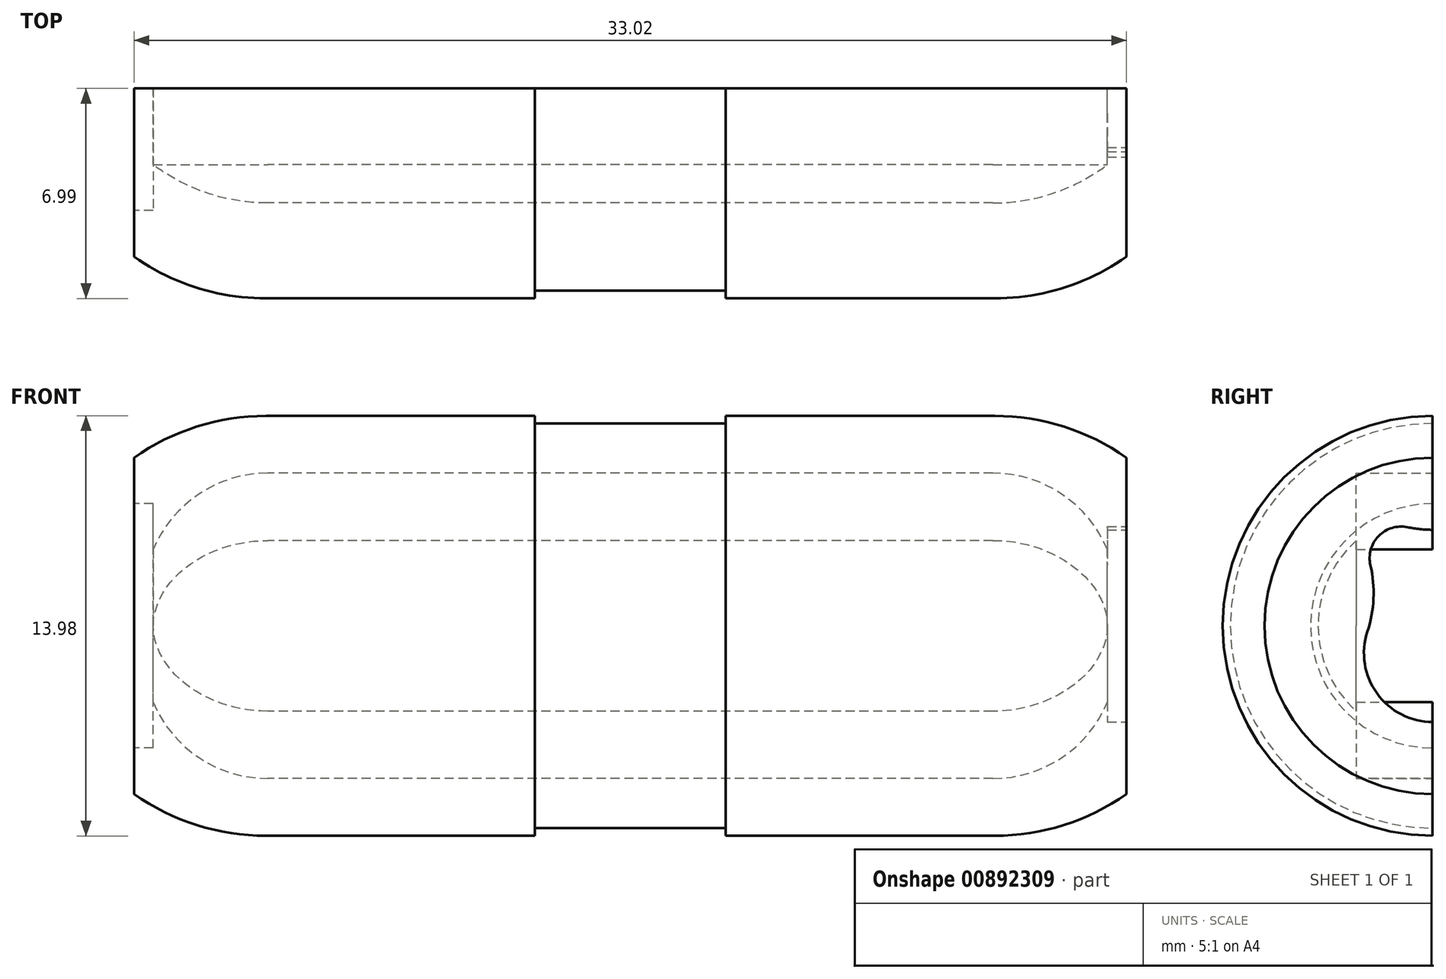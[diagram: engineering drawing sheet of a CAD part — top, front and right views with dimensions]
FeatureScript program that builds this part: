
annotation { "Feature Type Name" : "Feature", "Feature Type Description" : "" }
export const myFeature = defineFeature(function(context is Context, id is Id, definition is map)
    precondition{}
    {
        {
            var Q0;
            Q0=qCreatedBy(makeId("Front.planeOp"),FACE);
            var sketch = newSketch(context, id + "F0", { "sketchPlane" : qUnion([Q0])});
            skLineSegment(sketch, "E0.top", {"start": v(12.12, 6.99) * mm, "end": v(-12.12, 6.99) * mm});
            skPoint(sketch, "E0.middle", {"position": v(0, 0) * mm});
            skArc(sketch, "E1.filletArc", {"start": v(-12.12, 6.99) * mm, "mid": v(-16.24, 5.78) * mm, "end": v(-19.05, 2.54) * mm});
            skArc(sketch, "E2.filletArc", {"start": v(19.05, 2.54) * mm, "mid": v(16.24, 5.78) * mm, "end": v(12.12, 6.99) * mm});
            skLineSegment(sketch, "E3.top", {"start": v(12.07, 3.81) * mm, "end": v(-12.07, 3.81) * mm});
            skArc(sketch, "E4.filletArc", {"start": v(-12.07, 3.81) * mm, "mid": v(-14.07, 3.48) * mm, "end": v(-15.88, 2.54) * mm});
            skArc(sketch, "E5.filletArc", {"start": v(15.88, 2.54) * mm, "mid": v(14.07, 3.48) * mm, "end": v(12.07, 3.81) * mm});
            skLineSegment(sketch, "E6.top", {"start": v(-19.05, 2.54) * mm, "end": v(-15.88, 2.54) * mm});
            skLineSegment(sketch, "E7.trimOffspring", {"start": v(15.88, 2.54) * mm, "end": v(19.05, 2.54) * mm});
            skSolve(sketch);
        }
        {
            var Q0;
            Q0=qCreatedBy(makeId("Top.planeOp"),FACE);
            var sketch = newSketch(context, id + "F1", { "sketchPlane" : qUnion([Q0])});
            skLineSegment(sketch, "E8", {"start": v(-41.86, 0) * mm, "end": v(38.58, 0) * mm, "construction": true});
            skSolve(sketch);
        }
        {
            var Q0;
            Q0=qSketchRegion(id+"F0",true);
            var Q1;
            Q1=sQuery(id+"F1.wireOp",EDGE,"E8");
            revolve(context, id + "F2", {"surfaceOperationType" : NewSurfaceOperationType.NEW, "entities" : qUnion([Q0]), "axis" : qUnion([Q1]), "revolveType" : RevolveType.ONE_DIRECTION, "angle" : 180 * degree});
        }
        {
            var Q0;
            Q0=makeQuery(id+"F2.opRevolve","CAP_FACE",FACE,{"disambiguationData":[OSD([sQuery(id+"F0.wireOp",EDGE,"E0.top"),sQuery(id+"F0.wireOp",EDGE,"E1.filletArc"),sQuery(id+"F0.wireOp",EDGE,"E2.filletArc"),sQuery(id+"F0.wireOp",EDGE,"E3.top"),sQuery(id+"F0.wireOp",EDGE,"E4.filletArc"),sQuery(id+"F0.wireOp",EDGE,"E5.filletArc"),sQuery(id+"F0.wireOp",EDGE,"JIvlJlBu-vfLA-I6Gr-C8jU-59FBPmd7U8bv"),sQuery(id+"F0.wireOp",EDGE,"RInppC3X-QeJU-EZpC-KpJT-0cWvms3T49e7")])],"isStart":true});
            var sketch = newSketch(context, id + "F3", { "sketchPlane" : qUnion([Q0])});
            skPoint(sketch, "E9.middle", {"position": v(0, 0) * mm});
            skLineSegment(sketch, "E10", {"start": v(12.07, -3.8) * mm, "end": v(-12.07, -3.81) * mm});
            skLineSegment(sketch, "E11", {"start": v(-12.07, -3.81) * mm, "end": v(-12.07, -3.81) * mm});
            skLineSegment(sketch, "E12", {"start": v(-19.05, -12.7) * mm, "end": v(-19.05, -12.7) * mm});
            skArc(sketch, "E13", {"start": v(-12.07, -3.81) * mm, "mid": v(-14.07, -3.48) * mm, "end": v(-15.88, -2.54) * mm});
            skLineSegment(sketch, "E14", {"start": v(-12.07, -5.08) * mm, "end": v(12.07, -5.08) * mm});
            skLineSegment(sketch, "E15", {"start": v(-15.88, -2.54) * mm, "end": v(-15.88, -2.54) * mm});
            skPoint(sketch, "E16.visualSharp", {"position": v(-14.82, -5.08) * mm});
            skArc(sketch, "E16.filletArc", {"start": v(-15.88, -2.54) * mm, "mid": v(-14.35, -4.39) * mm, "end": v(-12.07, -5.08) * mm});
            skPoint(sketch, "E17.visualSharp", {"position": v(22.86, -7.62) * mm});
            skArc(sketch, "E17.filletArc", {"start": v(12.07, -5.08) * mm, "mid": v(14.35, -4.38) * mm, "end": v(15.88, -2.54) * mm});
            skArc(sketch, "E18", {"start": v(12.07, -3.81) * mm, "mid": v(14.07, -3.48) * mm, "end": v(15.88, -2.54) * mm});
            skArc(sketch, "E19.MirrorCS", {"start": v(12.07, 5.08) * mm, "mid": v(14.35, 4.38) * mm, "end": v(15.88, 2.54) * mm});
            skArc(sketch, "E20.MirrorCS", {"start": v(12.07, 3.81) * mm, "mid": v(14.07, 3.48) * mm, "end": v(15.88, 2.54) * mm});
            skLineSegment(sketch, "E21.MirrorCS", {"start": v(12.07, 3.8) * mm, "end": v(-12.07, 3.81) * mm});
            skLineSegment(sketch, "E22.MirrorCS", {"start": v(-12.07, 5.08) * mm, "end": v(12.07, 5.08) * mm});
            skArc(sketch, "E23.MirrorCS", {"start": v(-15.88, 2.54) * mm, "mid": v(-14.35, 4.39) * mm, "end": v(-12.07, 5.08) * mm});
            skArc(sketch, "E24.MirrorCS", {"start": v(-12.07, 3.81) * mm, "mid": v(-14.07, 3.48) * mm, "end": v(-15.88, 2.54) * mm});
            skSolve(sketch);
        }
        {
            var Q0;
            Q0=qSketchRegion(id+"F3",true);
            extrude(context, id + "F4", {"entities" : qUnion([Q0]), "operationType" : NewBodyOperationType.REMOVE, "oppositeDirection" : true, "depth" : 2.54 * mm, "offsetDistance" : 25.4 * mm});
        }
        {
            var Q0;
            Q0=qCreatedBy(makeId("Front.planeOp"),FACE);
            var sketch = newSketch(context, id + "F5", { "sketchPlane" : qUnion([Q0])});
            skLineSegment(sketch, "E25", {"start": v(48.97, 0) * mm, "end": v(-50.21, 0) * mm, "construction": true});
            skSolve(sketch);
        }
        {
            var Q0;
            Q0=makeQuery(id+"F2.opRevolve","CAP_FACE",FACE,{"disambiguationData":[OSD([sQuery(id+"F0.wireOp",EDGE,"E0.top"),sQuery(id+"F0.wireOp",EDGE,"E1.filletArc"),sQuery(id+"F0.wireOp",EDGE,"E2.filletArc"),sQuery(id+"F0.wireOp",EDGE,"E3.top"),sQuery(id+"F0.wireOp",EDGE,"E4.filletArc"),sQuery(id+"F0.wireOp",EDGE,"E5.filletArc"),sQuery(id+"F0.wireOp",EDGE,"E6.top"),sQuery(id+"F0.wireOp",EDGE,"E7.trimOffspring")])],"isStart":true});
            var sketch = newSketch(context, id + "F6", { "sketchPlane" : qUnion([Q0])});
            skLineSegment(sketch, "E26.bottom", {"start": v(3.18, 6.73) * mm, "end": v(-3.17, 6.73) * mm});
            skLineSegment(sketch, "E26.top", {"start": v(3.18, 7.24) * mm, "end": v(-3.17, 7.24) * mm});
            skLineSegment(sketch, "E26.left", {"start": v(3.18, 6.73) * mm, "end": v(3.18, 7.24) * mm});
            skLineSegment(sketch, "E26.right", {"start": v(-3.17, 6.73) * mm, "end": v(-3.17, 7.24) * mm});
            skPoint(sketch, "E26.middle", {"position": v(0, 6.99) * mm});
            skSolve(sketch);
        }
        {
            var Q0;
            Q0 = qSketchRegion(id + "F6", true);
            var Q1;
            Q1=sQuery(id+"F5.wireOp",EDGE,"E25");
            revolve(context, id + "F7", {"operationType" : NewBodyOperationType.REMOVE, "surfaceOperationType" : NewSurfaceOperationType.NEW, "entities" : qUnion([Q0]), "axis" : qUnion([Q1]), "revolveType" : RevolveType.FULL, "oppositeDirection" : true});
        }
        {
            var Q0;
            Q0=makeQuery(id+"F4.boolean.opBoolean","COPY",FACE,{"derivedFrom":makeQuery(id+"F4.opExtrude","CAP_FACE",FACE,{"disambiguationData":[OSD([sQuery(id+"F3.wireOp",EDGE,"E10"),sQuery(id+"F3.wireOp",EDGE,"E13"),sQuery(id+"F3.wireOp",EDGE,"E14"),sQuery(id+"F3.wireOp",EDGE,"L3rBEucQ-c3uq-OMWU-wc5G-qcBvpzBimpHX"),sQuery(id+"F3.wireOp",EDGE,"E16.filletArc"),sQuery(id+"F3.wireOp",EDGE,"19001bea-0d48-4adf-b7b1-09b1f723019d.filletArc")])],"isStart":false})});
            var sketch = newSketch(context, id + "F8", { "sketchPlane" : qUnion([Q0])});
            skLineSegment(sketch, "E27", {"start": v(-12.07, -3.3) * mm, "end": v(12.07, -3.3) * mm});
            skLineSegment(sketch, "E28", {"start": v(12.07, -3.8) * mm, "end": v(-12.07, -3.81) * mm});
            skPoint(sketch, "E29.visualSharp", {"position": v(-22.86, -12.7) * mm});
            skArc(sketch, "E29.filletArc", {"start": v(-15.88, -2.54) * mm, "mid": v(-14.07, -3.48) * mm, "end": v(-12.07, -3.81) * mm});
            skPoint(sketch, "E30.visualSharp", {"position": v(-15.88, -3.56) * mm});
            skArc(sketch, "E30.filletArc", {"start": v(-15.88, -1.78) * mm, "mid": v(-14.1, -2.86) * mm, "end": v(-12.07, -3.3) * mm});
            skPoint(sketch, "E31", {"position": v(-15.88, -1.78) * mm});
            skLineSegment(sketch, "E32", {"start": v(-15.88, -1.78) * mm, "end": v(-15.88, -2.54) * mm});
            skLineSegment(sketch, "E33", {"start": v(15.88, -2.54) * mm, "end": v(15.88, -2.54) * mm});
            skArc(sketch, "E34.filletArc", {"start": v(12.07, -3.8) * mm, "mid": v(14.07, -3.48) * mm, "end": v(15.88, -2.54) * mm});
            skLineSegment(sketch, "E35", {"start": v(15.88, -2.54) * mm, "end": v(15.88, -1.78) * mm});
            skLineSegment(sketch, "E36", {"start": v(12.07, -3.3) * mm, "end": v(12.07, -3.3) * mm});
            skPoint(sketch, "E37.visualSharp", {"position": v(15.88, -3.3) * mm});
            skArc(sketch, "E37.filletArc", {"start": v(12.07, -3.3) * mm, "mid": v(14.12, -2.9) * mm, "end": v(15.88, -1.78) * mm});
            skArc(sketch, "E38.MirrorCS", {"start": v(12.07, 3.8) * mm, "mid": v(14.07, 3.48) * mm, "end": v(15.88, 2.54) * mm});
            skArc(sketch, "E39.MirrorCS", {"start": v(12.07, 3.3) * mm, "mid": v(14.12, 2.9) * mm, "end": v(15.88, 1.78) * mm});
            skLineSegment(sketch, "E40.MirrorCS", {"start": v(15.88, 2.54) * mm, "end": v(15.88, 1.78) * mm});
            skLineSegment(sketch, "E41.MirrorCS", {"start": v(12.07, 3.8) * mm, "end": v(-12.07, 3.81) * mm});
            skLineSegment(sketch, "E42.MirrorCS", {"start": v(-15.88, 1.78) * mm, "end": v(-15.88, 2.54) * mm});
            skLineSegment(sketch, "E43.MirrorCS", {"start": v(-12.07, 3.3) * mm, "end": v(12.07, 3.3) * mm});
            skArc(sketch, "E44.MirrorCS", {"start": v(-15.88, 2.54) * mm, "mid": v(-14.07, 3.48) * mm, "end": v(-12.07, 3.81) * mm});
            skArc(sketch, "E45.MirrorCS", {"start": v(-15.88, 1.78) * mm, "mid": v(-14.1, 2.86) * mm, "end": v(-12.07, 3.3) * mm});
            skSolve(sketch);
        }
        {
            var Q0;
            Q0 = qSketchRegion(id + "F8", true);
            extrude(context, id + "F9", {"entities" : qUnion([Q0]), "operationType" : NewBodyOperationType.REMOVE, "depth" : 2.54 * mm, "offsetDistance" : 25.4 * mm});
        }
        {
            var Q0;
            Q0=makeQuery(id+"F2.opRevolve","CAP_FACE",FACE,{"disambiguationData":[OSD([sQuery(id+"F0.wireOp",EDGE,"E0.top"),sQuery(id+"F0.wireOp",EDGE,"E1.filletArc"),sQuery(id+"F0.wireOp",EDGE,"E2.filletArc"),sQuery(id+"F0.wireOp",EDGE,"E3.top"),sQuery(id+"F0.wireOp",EDGE,"E4.filletArc"),sQuery(id+"F0.wireOp",EDGE,"E5.filletArc"),sQuery(id+"F0.wireOp",EDGE,"E6.top"),sQuery(id+"F0.wireOp",EDGE,"E7.trimOffspring")])],"isStart":true});
            var sketch = newSketch(context, id + "F10", { "sketchPlane" : qUnion([Q0])});
            skLineSegment(sketch, "E46.bottom", {"start": v(-19.05, 5.6) * mm, "end": v(-16.51, 5.6) * mm});
            skLineSegment(sketch, "E46.top", {"start": v(-19.05, -5.6) * mm, "end": v(-16.51, -5.6) * mm});
            skLineSegment(sketch, "E46.left", {"start": v(-19.05, 5.6) * mm, "end": v(-19.05, -5.6) * mm});
            skLineSegment(sketch, "E46.right", {"start": v(-16.51, 5.6) * mm, "end": v(-16.51, -5.6) * mm});
            skLineSegment(sketch, "E47.MirrorCS", {"start": v(19.05, -5.6) * mm, "end": v(16.51, -5.6) * mm});
            skLineSegment(sketch, "E48.MirrorCS", {"start": v(19.05, 5.6) * mm, "end": v(19.05, -5.6) * mm});
            skLineSegment(sketch, "E49.MirrorCS", {"start": v(19.05, 5.6) * mm, "end": v(16.51, 5.6) * mm});
            skLineSegment(sketch, "E50.MirrorCS", {"start": v(16.51, 5.6) * mm, "end": v(16.51, -5.6) * mm});
            skSolve(sketch);
        }
        {
            var Q0;
            Q0 = qSketchRegion(id + "F10", true);
            extrude(context, id + "F11", {"entities" : qUnion([Q0]), "operationType" : NewBodyOperationType.REMOVE, "oppositeDirection" : true, "depth" : 25.4 * mm, "offsetDistance" : 25.4 * mm});
        }
        {
            var Q0;
            Q0=makeQuery(id+"F11.boolean.opBoolean","COPY",FACE,{"derivedFrom":makeQuery(id+"F11.opExtrude","SWEPT_FACE",FACE,{"disambiguationData":[OSD([sQuery(id+"F10.wireOp",EDGE,"E46.right")])]})});
            var sketch = newSketch(context, id + "F12", { "sketchPlane" : qUnion([Q0])});
            skArc(sketch, "E51", {"start": v(0, 2.54) * mm, "mid": v(-2.54, 0) * mm, "end": v(0, -2.54) * mm});
            skLineSegment(sketch, "E52", {"start": v(0, 2.54) * mm, "end": v(0, -2.54) * mm});
            skSolve(sketch);
        }
        {
            var Q0;
            Q0 = qSketchRegion(id + "F12", true);
            var Q1;
            {var subQ0=sQuery(id+"F0.wireOp",EDGE,"E7.trimOffspring");Q1=makeQuery(id+"F9.boolean.opBoolean","MERGE",VERTEX,{"derivedFrom":[makeQuery(id+"F4.boolean.opBoolean","MERGE",VERTEX,{"derivedFrom":[makeQuery(id+"F2.opRevolve","CAP_VERTEX",VERTEX,{"disambiguationData":[OSD([sQuery(id+"F0.wireOp",EDGE,"E5.filletArc"),subQ0])],"isStart":true})],"fromTools":[makeQuery(id+"F4.opExtrude","CAP_VERTEX",VERTEX,{"disambiguationData":[OSD([subQ0,sQuery(id+"F3.wireOp",EDGE,"24ab9741-bdfd-4dc7-9851-af407b64a0e66.MirrorCS"),sQuery(id+"F3.wireOp",EDGE,"24ab9741-bdfd-4dc7-9851-af407b64a0e67.MirrorCS")])],"isStart":true})]})],"fromTools":[makeQuery(id+"F9.opExtrude","CAP_VERTEX",VERTEX,{"disambiguationData":[OSD([sQuery(id+"F8.wireOp",EDGE,"E42.MirrorCS"),sQuery(id+"F8.wireOp",EDGE,"E44.MirrorCS")])],"isStart":false})]});}
            extrude(context, id + "F13", {"entities" : qUnion([Q0]), "operationType" : NewBodyOperationType.ADD, "endBound" : BoundingType.UP_TO_VERTEX, "oppositeDirection" : true, "depth" : 25.4 * mm, "endBoundEntityVertex" : qUnion([Q1]), "offsetDistance" : 25.4 * mm});
        }
        {
            var Q0;
            Q0=makeQuery(id+"F13.boolean.opBoolean","MERGE",FACE,{"derivedFrom":[makeQuery(id+"F11.boolean.opBoolean","COPY",FACE,{"derivedFrom":makeQuery(id+"F11.opExtrude","SWEPT_FACE",FACE,{"disambiguationData":[OSD([sQuery(id+"F10.wireOp",EDGE,"E46.right")])]})}),makeQuery(id+"F13.opExtrude","CAP_FACE",FACE,{"disambiguationData":[OSD([sQuery(id+"F12.wireOp",EDGE,"E51"),sQuery(id+"F12.wireOp",EDGE,"E52")])],"isStart":true})]});
            var sketch = newSketch(context, id + "F14", { "sketchPlane" : qUnion([Q0])});
            skArc(sketch, "E53", {"start": v(-2.17, -0.2) * mm, "mid": v(0, -3.2) * mm, "end": v(2.17, -0.2) * mm});
            skArc(sketch, "E54", {"start": v(2.07, 2.02) * mm, "mid": v(1.8, 2.99) * mm, "end": v(0.84, 3.28) * mm});
            skArc(sketch, "E55", {"start": v(-0.84, 3.28) * mm, "mid": v(-1.8, 2.99) * mm, "end": v(-2.07, 2.02) * mm});
            skPoint(sketch, "E56.visualSharp", {"position": v(-0.69, 1.27) * mm});
            skArc(sketch, "E56.filletArc", {"start": v(-2.17, -0.2) * mm, "mid": v(-1.97, 0.9) * mm, "end": v(-2.07, 2.02) * mm});
            skPoint(sketch, "E57.visualSharp", {"position": v(0, 2.25) * mm});
            skArc(sketch, "E57.filletArc", {"start": v(-0.84, 3.28) * mm, "mid": v(0, 3.2) * mm, "end": v(0.84, 3.28) * mm});
            skPoint(sketch, "E58.visualSharp", {"position": v(0.72, 1.26) * mm});
            skArc(sketch, "E58.filletArc", {"start": v(2.07, 2.02) * mm, "mid": v(1.97, 0.9) * mm, "end": v(2.17, -0.2) * mm});
            skLineSegment(sketch, "E59", {"start": v(0, -3.2) * mm, "end": v(0, 3.2) * mm, "construction": true});
            skPoint(sketch, "E59.endSnap0", {"position": v(0, 3.2) * mm});
            skPoint(sketch, "E60", {"position": v(0, 0) * mm});
            skSolve(sketch);
        }
        {
            var Q0;
            Q0 = qSketchRegion(id + "F14", true);
            var Q1;
            Q1=makeQuery(id+"F13.boolean.opBoolean","MERGE",FACE,{"derivedFrom":[makeQuery(id+"F9.boolean.opBoolean","COPY",FACE,{"derivedFrom":makeQuery(id+"F9.opExtrude","SWEPT_FACE",FACE,{"disambiguationData":[OSD([sQuery(id+"F8.wireOp",EDGE,"E32")])]})}),makeQuery(id+"F9.boolean.opBoolean","COPY",FACE,{"derivedFrom":makeQuery(id+"F9.opExtrude","SWEPT_FACE",FACE,{"disambiguationData":[OSD([sQuery(id+"F8.wireOp",EDGE,"E42.MirrorCS")])]})}),makeQuery(id+"F13.opExtrude","CAP_FACE",FACE,{"disambiguationData":[OSD([sQuery(id+"F12.wireOp",EDGE,"E51"),sQuery(id+"F12.wireOp",EDGE,"E52")])],"isStart":false})]});
            extrude(context, id + "F15", {"entities" : qUnion([Q0]), "operationType" : NewBodyOperationType.REMOVE, "endBound" : BoundingType.UP_TO_SURFACE, "oppositeDirection" : true, "depth" : 25.4 * mm, "endBoundEntityFace" : qUnion([Q1]), "offsetDistance" : 25.4 * mm});
        }
        {
            var Q0;
            Q0=makeQuery(id+"F11.boolean.opBoolean","COPY",FACE,{"derivedFrom":makeQuery(id+"F11.opExtrude","SWEPT_FACE",FACE,{"disambiguationData":[OSD([sQuery(id+"F10.wireOp",EDGE,"E50.MirrorCS")])]})});
            var sketch = newSketch(context, id + "F16", { "sketchPlane" : qUnion([Q0])});
            skArc(sketch, "E61", {"start": v(0, -2.54) * mm, "mid": v(2.54, 0) * mm, "end": v(0, 2.54) * mm});
            skLineSegment(sketch, "E62", {"start": v(0, 2.54) * mm, "end": v(0, -2.54) * mm});
            skSolve(sketch);
        }
        {
            var Q0;
            Q0 = qSketchRegion(id + "F16", true);
            var Q1;
            Q1=makeQuery(id+"F2.opRevolve","CAP_VERTEX",VERTEX,{"disambiguationData":[OSD([sQuery(id+"F0.wireOp",EDGE,"E4.filletArc"),sQuery(id+"F0.wireOp",EDGE,"E6.top")])],"isStart":true});
            extrude(context, id + "F17", {"entities" : qUnion([Q0]), "operationType" : NewBodyOperationType.ADD, "endBound" : BoundingType.UP_TO_VERTEX, "oppositeDirection" : true, "depth" : 25.4 * mm, "endBoundEntityVertex" : qUnion([Q1]), "offsetDistance" : 25.4 * mm});
        }
        {
            var Q0;
            Q0=makeQuery(id+"F17.boolean.opBoolean","MERGE",FACE,{"derivedFrom":[makeQuery(id+"F11.boolean.opBoolean","COPY",FACE,{"derivedFrom":makeQuery(id+"F11.opExtrude","SWEPT_FACE",FACE,{"disambiguationData":[OSD([sQuery(id+"F10.wireOp",EDGE,"E50.MirrorCS")])]})}),makeQuery(id+"F17.opExtrude","CAP_FACE",FACE,{"disambiguationData":[OSD([sQuery(id+"F16.wireOp",EDGE,"E61"),sQuery(id+"F16.wireOp",EDGE,"E62")])],"isStart":true})]});
            var sketch = newSketch(context, id + "F18", { "sketchPlane" : qUnion([Q0])});
            skCircle(sketch, "E63", {"center": v(0, 0) * mm, "radius": 4.06 * mm});
            skSolve(sketch);
        }
        {
            var Q0;
            Q0 = qSketchRegion(id + "F18", true);
            var Q1;
            Q1=makeQuery(id+"F17.opExtrude","CAP_FACE",FACE,{"disambiguationData":[OSD([sQuery(id+"F16.wireOp",EDGE,"E61"),sQuery(id+"F16.wireOp",EDGE,"E62")])],"isStart":false});
            extrude(context, id + "F19", {"entities" : qUnion([Q0]), "operationType" : NewBodyOperationType.REMOVE, "endBound" : BoundingType.UP_TO_SURFACE, "oppositeDirection" : true, "depth" : 25.4 * mm, "endBoundEntityFace" : qUnion([Q1]), "offsetDistance" : 25.4 * mm});
        }
        {
            var Q0;
            Q0=makeQuery(id+"F9.boolean.opBoolean","MERGE",FACE,{"derivedFrom":[makeQuery(id+"F4.boolean.opBoolean","COPY",FACE,{"derivedFrom":makeQuery(id+"F4.opExtrude","CAP_FACE",FACE,{"disambiguationData":[OSD([sQuery(id+"F3.wireOp",EDGE,"E19.MirrorCS"),sQuery(id+"F3.wireOp",EDGE,"E20.MirrorCS"),sQuery(id+"F3.wireOp",EDGE,"E21.MirrorCS"),sQuery(id+"F3.wireOp",EDGE,"E22.MirrorCS"),sQuery(id+"F3.wireOp",EDGE,"E23.MirrorCS"),sQuery(id+"F3.wireOp",EDGE,"E24.MirrorCS")])],"isStart":false})})],"fromTools":[makeQuery(id+"F9.opExtrude","CAP_FACE",FACE,{"disambiguationData":[OSD([sQuery(id+"F8.wireOp",EDGE,"E38.MirrorCS"),sQuery(id+"F8.wireOp",EDGE,"E39.MirrorCS"),sQuery(id+"F8.wireOp",EDGE,"E40.MirrorCS"),sQuery(id+"F8.wireOp",EDGE,"E41.MirrorCS"),sQuery(id+"F8.wireOp",EDGE,"E42.MirrorCS"),sQuery(id+"F8.wireOp",EDGE,"E43.MirrorCS"),sQuery(id+"F8.wireOp",EDGE,"E44.MirrorCS"),sQuery(id+"F8.wireOp",EDGE,"E45.MirrorCS")])],"isStart":true})]});
            var sketch = newSketch(context, id + "F20", { "sketchPlane" : qUnion([Q0])});
            skLineSegment(sketch, "E64", {"start": v(-12.07, 5.08) * mm, "end": v(12.07, 5.08) * mm});
            skArc(sketch, "E65", {"start": v(15.88, 2.54) * mm, "mid": v(14.35, 4.39) * mm, "end": v(12.06, 5.08) * mm});
            skLineSegment(sketch, "E66", {"start": v(15.88, 2.54) * mm, "end": v(15.88, -2.54) * mm});
            skArc(sketch, "E67", {"start": v(12.06, -5.08) * mm, "mid": v(14.35, -4.39) * mm, "end": v(15.87, -2.54) * mm});
            skLineSegment(sketch, "E68", {"start": v(12.06, -5.08) * mm, "end": v(-12.07, -5.08) * mm});
            skArc(sketch, "E69", {"start": v(-12.07, 5.08) * mm, "mid": v(-14.35, 4.39) * mm, "end": v(-15.88, 2.54) * mm});
            skArc(sketch, "E70", {"start": v(-15.88, -2.54) * mm, "mid": v(-14.35, -4.39) * mm, "end": v(-12.07, -5.08) * mm});
            skPoint(sketch, "E71.orphan", {"position": v(15.88, -3.3) * mm});
            skLineSegment(sketch, "E72", {"start": v(-15.88, 2.54) * mm, "end": v(-15.88, -2.54) * mm});
            skSolve(sketch);
        }
        {
            var Q0;
            Q0 = qSketchRegion(id + "F20", true);
            var Q1;
            {var subQ5=sQuery(id+"F0.wireOp",EDGE,"E0.top");var subQ8=sQuery(id+"F0.wireOp",EDGE,"E1.filletArc");var subQ10=sQuery(id+"F0.wireOp",EDGE,"E7.trimOffspring");var subQ11=sQuery(id+"F0.wireOp",EDGE,"E6.top");var subQ12=sQuery(id+"F0.wireOp",EDGE,"E5.filletArc");var subQ13=sQuery(id+"F0.wireOp",EDGE,"E4.filletArc");var subQ14=sQuery(id+"F0.wireOp",EDGE,"E3.top");var subQ15=sQuery(id+"F0.wireOp",EDGE,"E2.filletArc");var subQ16=makeQuery(id+"F2.opRevolve","CAP_FACE",FACE,{"disambiguationData":[OSD([subQ5,subQ8,subQ15,subQ14,subQ13,subQ12,subQ11,subQ10])],"isStart":true});var subQ17=makeQuery(id+"F2.opRevolve","CAP_FACE",FACE,{"disambiguationData":[OSD([subQ5,subQ8,subQ15,subQ14,subQ13,subQ12,subQ11,subQ10])],"isStart":false});var subQ18=sQuery(id+"F12.wireOp",EDGE,"E52");var subQ21=makeQuery(id+"F13.opExtrude","SWEPT_FACE",FACE,{"disambiguationData":[OSD([subQ18])]});var subQ28=sQuery(id+"F16.wireOp",EDGE,"E62");var subQ29=makeQuery(id+"F4.boolean.opBoolean","COPY",FACE,{"derivedFrom":makeQuery(id+"F4.opExtrude","SWEPT_FACE",FACE,{"disambiguationData":[OSD([sQuery(id+"F3.wireOp",EDGE,"E19.MirrorCS")])]})});var subQ33=makeQuery(id+"F13.boolean.opBoolean","MERGE",FACE,{"derivedFrom":[subQ16,subQ17,subQ21]});Q1=makeQuery(id+"F19.boolean.opBoolean","SPLIT",FACE,{"disambiguationData":[TD([subQ29])],"derivedFrom":makeQuery(id+"F17.boolean.opBoolean","MERGE",FACE,{"derivedFrom":[makeQuery(id+"F15.boolean.opBoolean","SPLIT",FACE,{"disambiguationData":[TD([makeQuery(id+"F4.boolean.opBoolean","COPY",FACE,{"derivedFrom":makeQuery(id+"F4.opExtrude","SWEPT_FACE",FACE,{"disambiguationData":[OSD([sQuery(id+"F3.wireOp",EDGE,"E14")])]})})])],"derivedFrom":subQ33}),makeQuery(id+"F15.boolean.opBoolean","SPLIT",FACE,{"disambiguationData":[TD([subQ29])],"derivedFrom":subQ33}),makeQuery(id+"F17.opExtrude","SWEPT_FACE",FACE,{"disambiguationData":[OSD([subQ28])]})]})});}
            extrude(context, id + "F21", {"entities" : qUnion([Q0]), "operationType" : NewBodyOperationType.REMOVE, "endBound" : BoundingType.UP_TO_SURFACE, "depth" : 25.4 * mm, "endBoundEntityFace" : qUnion([Q1]), "offsetDistance" : 25.4 * mm});
        }
    });
